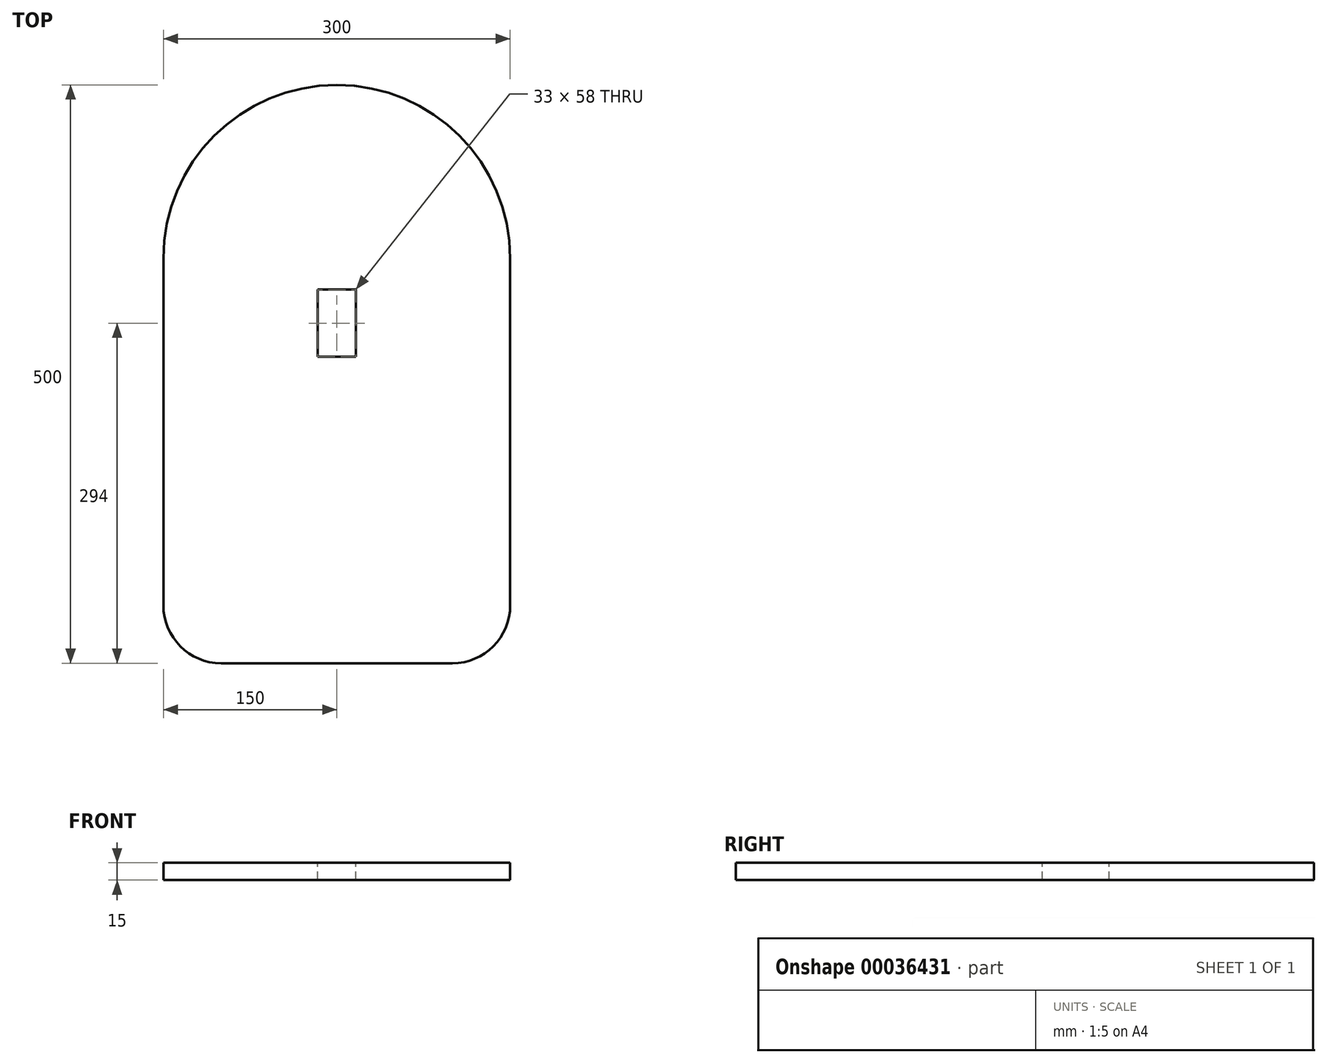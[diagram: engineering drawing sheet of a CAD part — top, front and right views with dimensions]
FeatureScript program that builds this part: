
annotation { "Feature Type Name" : "Feature", "Feature Type Description" : "" }
export const myFeature = defineFeature(function(context is Context, id is Id, definition is map)
    precondition{}
    {
        {
            var Q0;
            Q0=qCreatedBy(makeId("Top.planeOp"),FACE);
            var sketch = newSketch(context, id + "F0", { "sketchPlane" : qUnion([Q0])});
            skLineSegment(sketch, "E0.rect.bottom", {"start": v(100, -250) * mm, "end": v(-100, -250) * mm});
            skLineSegment(sketch, "E0.rect.left", {"start": v(150, -200) * mm, "end": v(150, 100) * mm});
            skLineSegment(sketch, "E0.rect.right", {"start": v(-150, -250) * mm, "end": v(-150, 100) * mm});
            skPoint(sketch, "E0.rect.middle", {"position": v(0, 0) * mm});
            skPoint(sketch, "E1.orphan", {"position": v(-150, 250) * mm});
            skPoint(sketch, "E2.orphan", {"position": v(150, 250) * mm});
            skArc(sketch, "E3", {"start": v(150, 100) * mm, "mid": v(0, 250) * mm, "end": v(-150, 100) * mm});
            skPoint(sketch, "E4.start.orphan", {"position": v(0, 250) * mm});
            skPoint(sketch, "E5.start.orphan", {"position": v(-100, 250) * mm});
            skPoint(sketch, "E6.end.orphan", {"position": v(100, 250) * mm});
            skArc(sketch, "E7", {"start": v(-150, -200) * mm, "mid": v(-135.36, -235.36) * mm, "end": v(-100, -250) * mm});
            skArc(sketch, "E8", {"start": v(100, -250) * mm, "mid": v(135.36, -235.36) * mm, "end": v(150, -200) * mm});
            skPoint(sketch, "E9.orphan", {"position": v(150, -250) * mm});
            skSolve(sketch);
        }
        {
            var Q0;
            Q0 = qSketchRegion(id + "F0", true);
            extrude(context, id + "F1", {"entities" : qUnion([Q0]), "depth" : 15 * mm});
        }
        {
            var Q0;
            Q0=makeQuery(id+"F1.opExtrude","CAP_FACE",FACE,{"disambiguationData":[OSD([sQuery(id+"F0.wireOp",EDGE,"E0.rect.bottom"),sQuery(id+"F0.wireOp",EDGE,"E0.rect.left"),sQuery(id+"F0.wireOp",EDGE,"E0.rect.right"),sQuery(id+"F0.wireOp",EDGE,"E3"),sQuery(id+"F0.wireOp",EDGE,"E7"),sQuery(id+"F0.wireOp",EDGE,"E8")])],"isStart":false});
            var sketch = newSketch(context, id + "F2", { "sketchPlane" : qUnion([Q0])});
            skLineSegment(sketch, "E10.bottom", {"start": v(-16.5, 73) * mm, "end": v(16.5, 73) * mm});
            skLineSegment(sketch, "E10.top", {"start": v(-16.5, 15) * mm, "end": v(16.5, 15) * mm});
            skLineSegment(sketch, "E10.left", {"start": v(-16.5, 73) * mm, "end": v(-16.5, 15) * mm});
            skLineSegment(sketch, "E10.right", {"start": v(16.5, 73) * mm, "end": v(16.5, 15) * mm});
            skLineSegment(sketch, "E11", {"start": v(150, 100) * mm, "end": v(-52.78, 100) * mm});
            skSolve(sketch);
        }
        {
            var Q0;
            Q0 = qSketchRegion(id + "F2", true);
            extrude(context, id + "F3", {"entities" : qUnion([Q0]), "operationType" : NewBodyOperationType.REMOVE, "endBound" : BoundingType.THROUGH_ALL, "oppositeDirection" : true, "depth" : 25 * mm});
        }
    });
